# Revit family: Shower-Bath_Shower-KOHLER-ALEO-K-25109T_1
name_source: partatom
category: Plumbing Fixtures
units: mm (PartAtom-declared; Revit-internal decimal feet)

## family parameters
Cut with Voids When Loaded = No
Host = Face
OmniClass Number = 23.31.17.00
OmniClass Title = Showers
Part Type = Normal
Room Calculation Point = No
Round Connector Dimension = Use Diameter
Shared = No

## types (3) — shared parameters
ADA Compliant = No
Assembly Code = D2010700
CW Connection = Yes
Cold Water Inlet = Cold Water Inlet
Date Modified = 08/08/2022
Default Elevation = 36"
Description = Wall-mounted thermostatic bathtub shower faucet (ingenious style)
Drain Included = No
Flow Rate = 0 GPM
HW Connection = Yes
Height = 34 1/8"
Hot Water Inlet = Hot Water Inlet
Length = 7 11/16"
Manufacturer = Kohler Co.
Master Format 2014 = 22 42 23
Master Format 2014 Name = Residential Showers
Material = Premium Metal Construction
Pressure = 72.52 psi
Product Documentation Link = https://files.kohler.com.cn
Product Name = ALEO
Product Page URL = https://www.kohler.com.cn
Spout Reach = 7 11/16"
URL = http://www.kohler.com.cn
Vent Connection = No
Waste Connection = No
Waste Water Outlet = Waste Water Outlet
WaterSense Certified = No
Width = 5 15/16"

## per-type parameters (varying)
| type | Finish | Model | Type |
| CP-Polished Chrome | Kohler-Metal-CP-Polished_Chrome | K-25109T-9-CP | 1 |
| 2BL-Black | KOHLER-Metal-2BL-Black | K-25109T-9-2BL | 2 |
| BL-Matte Black | Kohler-Metal-BL-Matte_Black | K-25109T-9-BL | 3 |

## geometry (parser evidence)
native form markers: Sweep x6
no freeform markers — native parametric forms only
